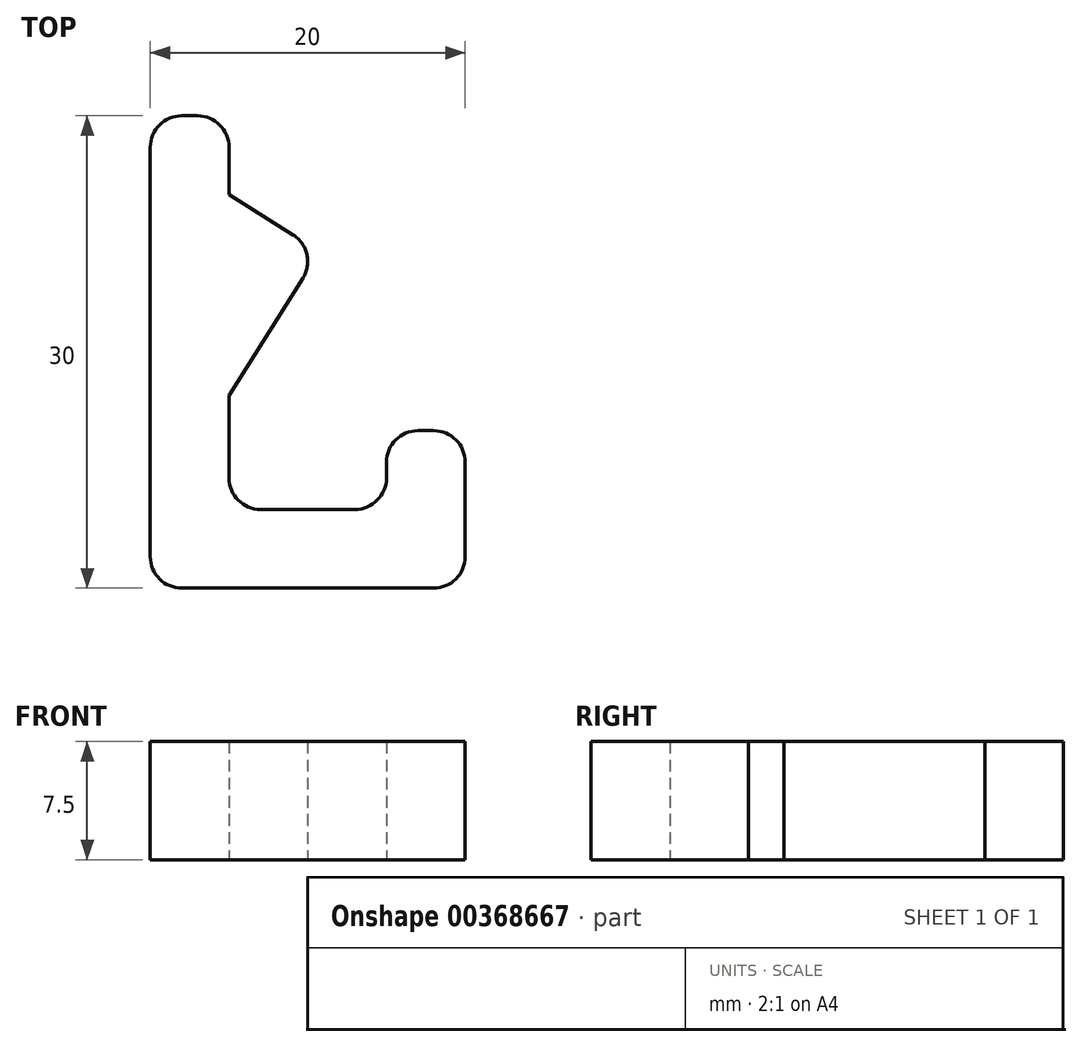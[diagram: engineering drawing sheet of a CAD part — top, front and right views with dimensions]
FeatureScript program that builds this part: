
annotation { "Feature Type Name" : "Feature", "Feature Type Description" : "" }
export const myFeature = defineFeature(function(context is Context, id is Id, definition is map)
    precondition{}
    {
        {
            var Q0;
            Q0=qCreatedBy(makeId("Top.planeOp"),FACE);
            var sketch = newSketch(context, id + "F0", { "sketchPlane" : qUnion([Q0])});
            skLineSegment(sketch, "E0", {"start": v(-20, 28) * mm, "end": v(-20, 2) * mm});
            skLineSegment(sketch, "E1", {"start": v(-18, 0) * mm, "end": v(-2, 0) * mm});
            skLineSegment(sketch, "E2", {"start": v(0, 2) * mm, "end": v(0, 8) * mm});
            skLineSegment(sketch, "E3.0", {"start": v(-5, 7) * mm, "end": v(-5, 8) * mm});
            skLineSegment(sketch, "E3.1", {"start": v(-13, 5) * mm, "end": v(-7, 5) * mm});
            skLineSegment(sketch, "E3.2", {"start": v(-15, 12.23) * mm, "end": v(-15, 7) * mm});
            skLineSegment(sketch, "E4", {"start": v(-15, 25) * mm, "end": v(-10.93, 22.44) * mm});
            skLineSegment(sketch, "E5", {"start": v(-10.3, 19.68) * mm, "end": v(-15, 12.23) * mm});
            skPoint(sketch, "E6.visualSharp", {"position": v(-9.24, 21.37) * mm});
            skArc(sketch, "E6.filletArc", {"start": v(-10.3, 19.68) * mm, "mid": v(-10.05, 21.19) * mm, "end": v(-10.93, 22.44) * mm});
            skLineSegment(sketch, "E7", {"start": v(-10, 30.83) * mm, "end": v(-10, 20.41) * mm, "construction": true});
            skLineSegment(sketch, "E8", {"start": v(-15, 25) * mm, "end": v(-15, 28) * mm});
            skLineSegment(sketch, "E9", {"start": v(-17, 30) * mm, "end": v(-18, 30) * mm});
            skLineSegment(sketch, "E10", {"start": v(-2, 10) * mm, "end": v(-3, 10) * mm});
            skPoint(sketch, "E11.visualSharp", {"position": v(-20, 0) * mm});
            skArc(sketch, "E11.filletArc", {"start": v(-20, 2) * mm, "mid": v(-19.41, 0.59) * mm, "end": v(-18, 0) * mm});
            skPoint(sketch, "E12.visualSharp", {"position": v(-15, 5) * mm});
            skArc(sketch, "E12.filletArc", {"start": v(-15, 7) * mm, "mid": v(-14.41, 5.59) * mm, "end": v(-13, 5) * mm});
            skPoint(sketch, "E13.visualSharp", {"position": v(-5, 5) * mm});
            skArc(sketch, "E13.filletArc", {"start": v(-7, 5) * mm, "mid": v(-5.59, 5.59) * mm, "end": v(-5, 7) * mm});
            skPoint(sketch, "E14.visualSharp", {"position": v(0, 0) * mm});
            skArc(sketch, "E14.filletArc", {"start": v(-2, 0) * mm, "mid": v(-0.59, 0.59) * mm, "end": v(0, 2) * mm});
            skPoint(sketch, "E15.visualSharp", {"position": v(-20, 30) * mm});
            skArc(sketch, "E15.filletArc", {"start": v(-18, 30) * mm, "mid": v(-19.41, 29.41) * mm, "end": v(-20, 28) * mm});
            skPoint(sketch, "E16.visualSharp", {"position": v(-15, 30) * mm});
            skArc(sketch, "E16.filletArc", {"start": v(-15, 28) * mm, "mid": v(-15.59, 29.41) * mm, "end": v(-17, 30) * mm});
            skPoint(sketch, "E17.visualSharp", {"position": v(0, 10) * mm});
            skArc(sketch, "E17.filletArc", {"start": v(0, 8) * mm, "mid": v(-0.59, 9.41) * mm, "end": v(-2, 10) * mm});
            skPoint(sketch, "E18.visualSharp", {"position": v(-5, 10) * mm});
            skArc(sketch, "E18.filletArc", {"start": v(-3, 10) * mm, "mid": v(-4.41, 9.41) * mm, "end": v(-5, 8) * mm});
            skSolve(sketch);
        }
        {
            var Q0;
            Q0=makeQuery(id+"F0.imprint","IMPRINT",FACE,{"disambiguationData":[TD([[makeQuery(id+"F0.imprint","IMPRINT",EDGE,{"derivedFrom":sQuery(id+"F0.wireOp",EDGE,"E0")}),1.0]])]});
            extrude(context, id + "F1", {"entities" : qUnion([Q0]), "depth" : 7.5 * mm});
        }
    });
